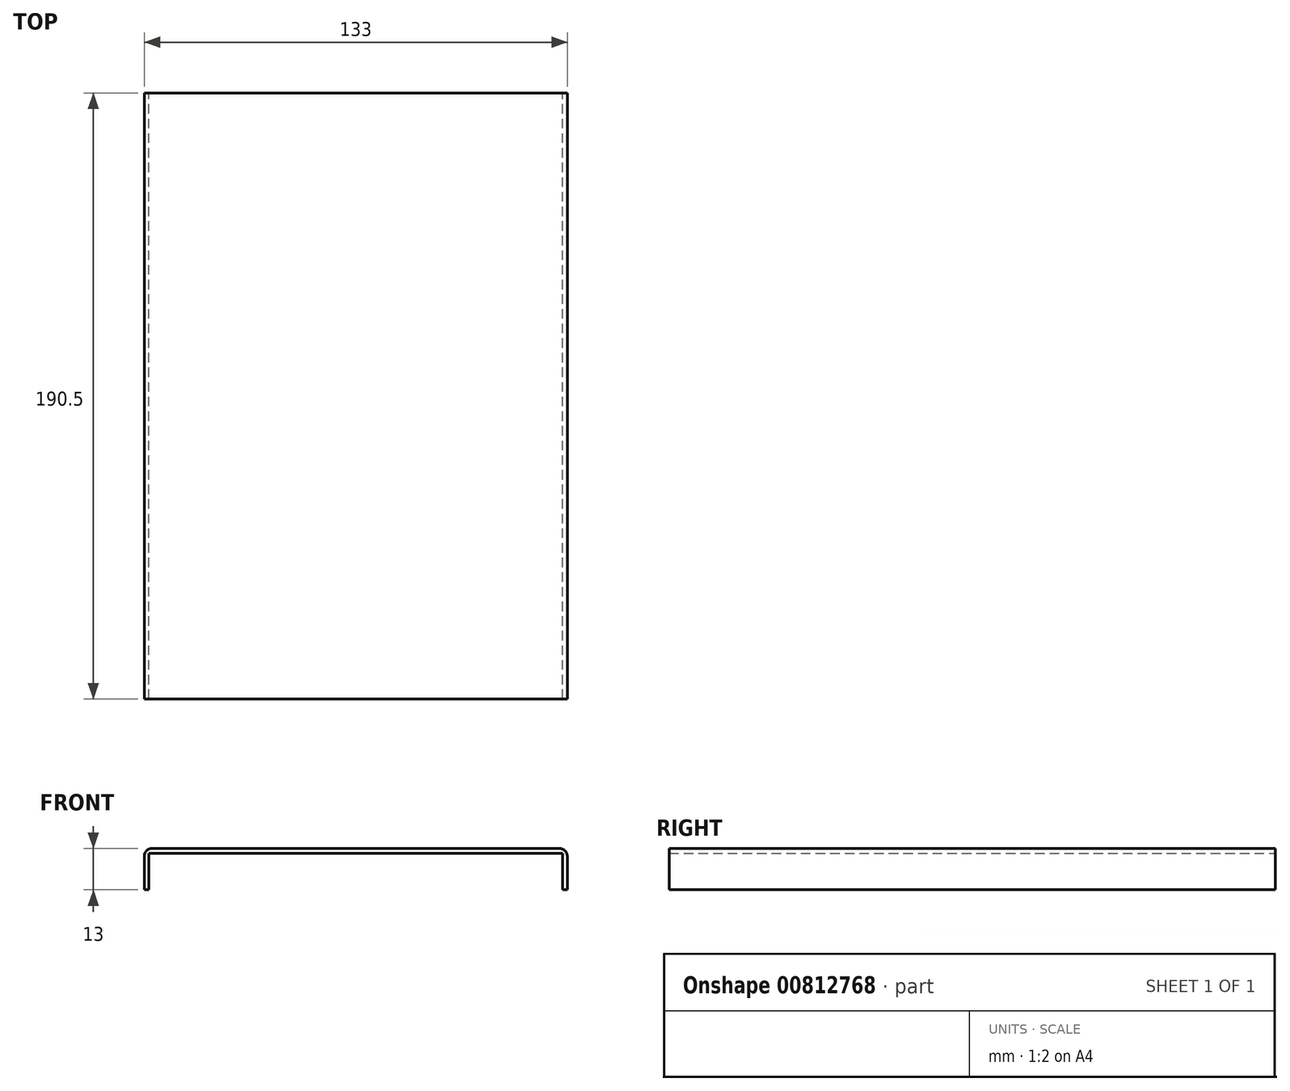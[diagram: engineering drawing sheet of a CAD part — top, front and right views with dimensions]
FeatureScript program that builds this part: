
annotation { "Feature Type Name" : "Feature", "Feature Type Description" : "" }
export const myFeature = defineFeature(function(context is Context, id is Id, definition is map)
    precondition{}
    {
        {
            var Q0;
            Q0=qCreatedBy(makeId("Front.planeOp"),FACE);
            var sketch = newSketch(context, id + "F0", { "sketchPlane" : qUnion([Q0])});
            skLineSegment(sketch, "E0", {"start": v(0, 0) * mm, "end": v(0, 10.5) * mm});
            skLineSegment(sketch, "E1", {"start": v(2.5, 13) * mm, "end": v(130.5, 13) * mm});
            skLineSegment(sketch, "E2", {"start": v(133, 10.5) * mm, "end": v(133, 0) * mm});
            skLineSegment(sketch, "E3", {"start": v(133, 0) * mm, "end": v(131.5, 0) * mm});
            skLineSegment(sketch, "E4", {"start": v(131.5, 0) * mm, "end": v(131.5, 11.5) * mm});
            skLineSegment(sketch, "E5", {"start": v(131.5, 11.5) * mm, "end": v(1.5, 11.5) * mm});
            skLineSegment(sketch, "E6", {"start": v(1.5, 11.5) * mm, "end": v(1.5, 0) * mm});
            skLineSegment(sketch, "E7", {"start": v(1.5, 0) * mm, "end": v(0, 0) * mm});
            skPoint(sketch, "E8.visualSharp", {"position": v(133, 13) * mm});
            skArc(sketch, "E8.filletArc", {"start": v(133, 10.5) * mm, "mid": v(132.27, 12.27) * mm, "end": v(130.5, 13) * mm});
            skPoint(sketch, "E9.visualSharp", {"position": v(0, 13) * mm});
            skArc(sketch, "E9.filletArc", {"start": v(2.5, 13) * mm, "mid": v(0.73, 12.27) * mm, "end": v(0, 10.5) * mm});
            skSolve(sketch);
        }
        {
            var Q0;
            Q0=makeQuery(id+"F0.imprint","IMPRINT",FACE,{"disambiguationData":[TD([[makeQuery(id+"F0.imprint","IMPRINT",EDGE,{"derivedFrom":sQuery(id+"F0.wireOp",EDGE,"E0")}),-1.0]])]});
            extrude(context, id + "F1", {"entities" : qUnion([Q0]), "depth" : 190.5 * mm, "offsetDistance" : 25 * mm});
        }
    });
